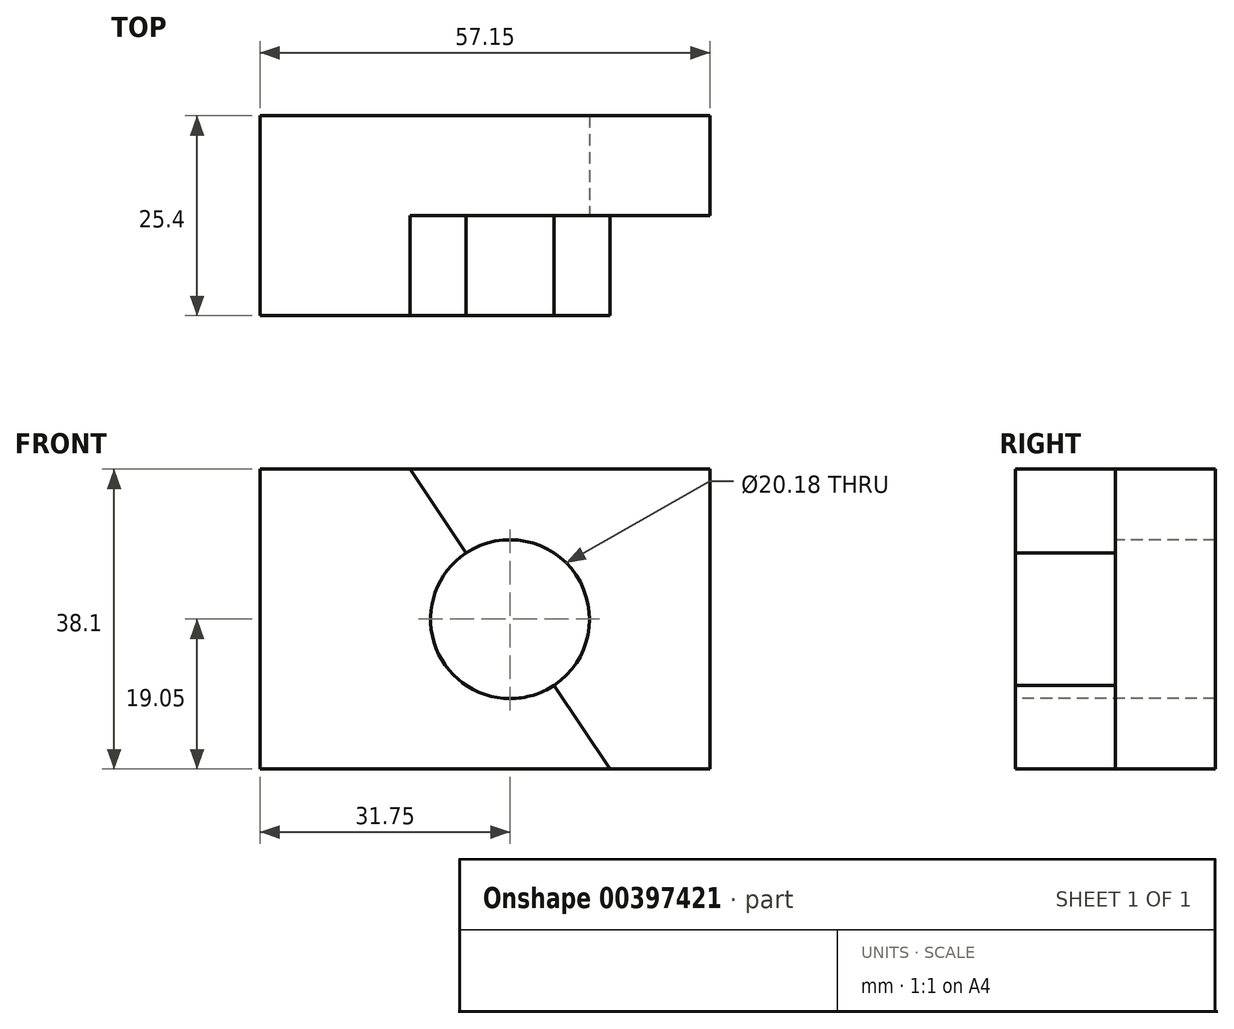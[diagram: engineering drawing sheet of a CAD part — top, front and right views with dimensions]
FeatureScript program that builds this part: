
annotation { "Feature Type Name" : "Feature", "Feature Type Description" : "" }
export const myFeature = defineFeature(function(context is Context, id is Id, definition is map)
    precondition{}
    {
        {
            var Q0;
            Q0=qCreatedBy(makeId("Front.planeOp"),FACE);
            var sketch = newSketch(context, id + "F0", { "sketchPlane" : qUnion([Q0])});
            skLineSegment(sketch, "E0", {"start": v(0, 38.1) * mm, "end": v(0, 0) * mm});
            skLineSegment(sketch, "E1", {"start": v(0, 0) * mm, "end": v(57.15, 0) * mm});
            skLineSegment(sketch, "E2", {"start": v(57.15, 0) * mm, "end": v(57.15, 38.1) * mm});
            skLineSegment(sketch, "E3", {"start": v(57.15, 38.1) * mm, "end": v(0, 38.1) * mm});
            skSolve(sketch);
        }
        {
            var Q0;
            Q0 = qSketchRegion(id + "F0", true);
            extrude(context, id + "F1", {"entities" : qUnion([Q0]), "depth" : 12.7 * mm});
        }
        {
            var Q0;
            Q0=makeQuery(id+"F1.opExtrude","CAP_FACE",FACE,{"disambiguationData":[OSD([sQuery(id+"F0.wireOp",EDGE,"E0"),sQuery(id+"F0.wireOp",EDGE,"E1"),sQuery(id+"F0.wireOp",EDGE,"E2"),sQuery(id+"F0.wireOp",EDGE,"E3")])],"isStart":false});
            var sketch = newSketch(context, id + "F2", { "sketchPlane" : qUnion([Q0])});
            skLineSegment(sketch, "E4", {"start": v(0, 38.1) * mm, "end": v(19.05, 38.1) * mm});
            skLineSegment(sketch, "E5", {"start": v(19.05, 38.1) * mm, "end": v(44.45, 0) * mm});
            skLineSegment(sketch, "E6", {"start": v(44.45, 0) * mm, "end": v(0, 0) * mm});
            skLineSegment(sketch, "E7", {"start": v(0, 0) * mm, "end": v(0, 38.1) * mm});
            skSolve(sketch);
        }
        {
            var Q0;
            Q0=makeQuery(id+"F2.imprint","IMPRINT",FACE,{"disambiguationData":[TD([[makeQuery(id+"F2.imprint","IMPRINT",EDGE,{"derivedFrom":sQuery(id+"F2.wireOp",EDGE,"E4")}),1.0]])]});
            extrude(context, id + "F3", {"entities" : qUnion([Q0]), "operationType" : NewBodyOperationType.ADD, "depth" : 12.7 * mm});
        }
        {
            var Q0;
            Q0=makeQuery(id+"F3.opExtrude","CAP_FACE",FACE,{"disambiguationData":[OSD([sQuery(id+"F2.wireOp",EDGE,"E4"),sQuery(id+"F2.wireOp",EDGE,"E5"),sQuery(id+"F2.wireOp",EDGE,"E6"),sQuery(id+"F2.wireOp",EDGE,"E7")])],"isStart":false});
            var sketch = newSketch(context, id + "F4", { "sketchPlane" : qUnion([Q0])});
            skCircle(sketch, "E8", {"center": v(31.75, 19.05) * mm, "radius": 10.1 * mm});
            skSolve(sketch);
        }
        {
            var Q0;
            Q0 = qSketchRegion(id + "F4", true);
            extrude(context, id + "F5", {"entities" : qUnion([Q0]), "operationType" : NewBodyOperationType.REMOVE, "oppositeDirection" : true, "depth" : 25.4 * mm});
        }
    });
